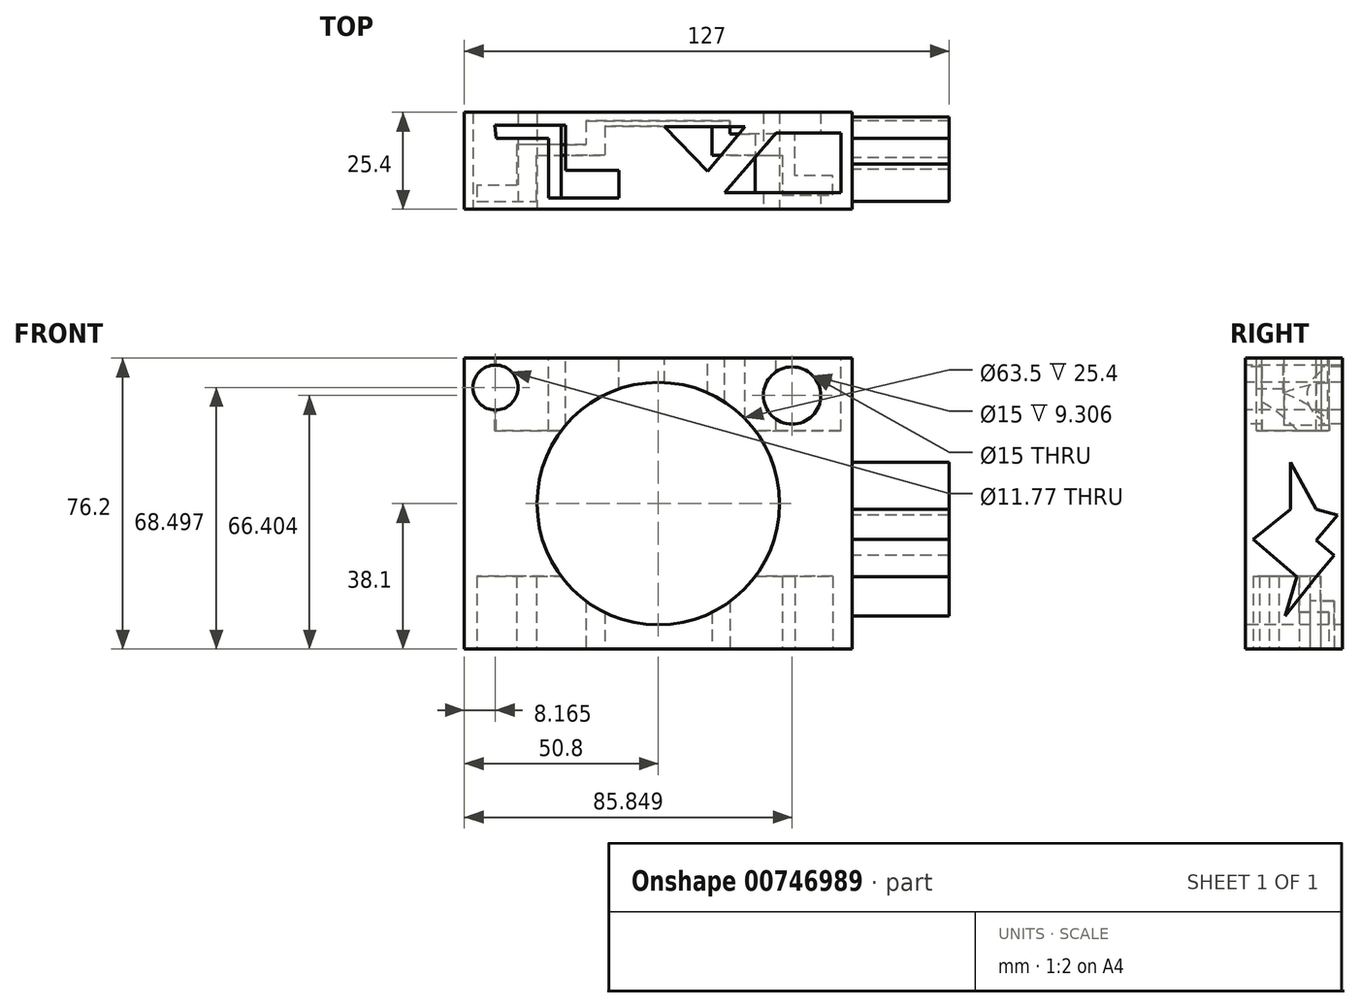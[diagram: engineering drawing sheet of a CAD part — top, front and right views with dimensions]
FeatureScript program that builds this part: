
annotation { "Feature Type Name" : "Feature", "Feature Type Description" : "" }
export const myFeature = defineFeature(function(context is Context, id is Id, definition is map)
    precondition{}
    {
        {
            var Q0;
            Q0=qCreatedBy(makeId("Front.planeOp"),FACE);
            var sketch = newSketch(context, id + "F0", { "sketchPlane" : qUnion([Q0])});
            skLineSegment(sketch, "E0.bottom", {"start": v(0, 0) * mm, "end": v(101.6, 0) * mm});
            skLineSegment(sketch, "E0.top", {"start": v(0, 76.2) * mm, "end": v(101.6, 76.2) * mm});
            skLineSegment(sketch, "E0.left", {"start": v(0, 0) * mm, "end": v(0, 76.2) * mm});
            skLineSegment(sketch, "E0.right", {"start": v(101.6, 0) * mm, "end": v(101.6, 76.2) * mm});
            skSolve(sketch);
        }
        {
            var Q0;
            Q0 = qSketchRegion(id + "F0", true);
            extrude(context, id + "F1", {"entities" : qUnion([Q0]), "depth" : 25.4 * mm, "offsetDistance" : 25.4 * mm});
        }
        {
            var Q0;
            Q0=makeQuery(id+"F1.opExtrude","CAP_FACE",FACE,{"disambiguationData":[OSD([sQuery(id+"F0.wireOp",EDGE,"E0.bottom"),sQuery(id+"F0.wireOp",EDGE,"E0.top"),sQuery(id+"F0.wireOp",EDGE,"E0.left"),sQuery(id+"F0.wireOp",EDGE,"E0.right")])],"isStart":false});
            var sketch = newSketch(context, id + "F2", { "sketchPlane" : qUnion([Q0])});
            skCircle(sketch, "E1", {"center": v(50.8, 38.1) * mm, "radius": 31.75 * mm});
            skPoint(sketch, "E1.centerSnap0", {"position": v(0, 38.1) * mm});
            skSolve(sketch);
        }
        {
            var Q0;
            Q0 = qSketchRegion(id + "F2", true);
            extrude(context, id + "F3", {"entities" : qUnion([Q0]), "operationType" : NewBodyOperationType.ADD, "depth" : 25.4 * mm, "offsetDistance" : 25.4 * mm});
        }
        {
            var Q0;
            Q0=makeQuery(id+"F3.opExtrude","CAP_FACE",FACE,{"disambiguationData":[OSD([sQuery(id+"F2.wireOp",EDGE,"E1")])],"isStart":false});
            extrude(context, id + "F4", {"entities" : qUnion([Q0]), "operationType" : NewBodyOperationType.REMOVE, "endBound" : BoundingType.THROUGH_ALL, "oppositeDirection" : true, "depth" : 25.4 * mm, "offsetDistance" : 25.4 * mm});
        }
        {
            var Q0;
            Q0=makeQuery(id+"F1.opExtrude","CAP_FACE",FACE,{"disambiguationData":[OSD([sQuery(id+"F0.wireOp",EDGE,"E0.bottom"),sQuery(id+"F0.wireOp",EDGE,"E0.top"),sQuery(id+"F0.wireOp",EDGE,"E0.left"),sQuery(id+"F0.wireOp",EDGE,"E0.right")])],"isStart":false});
            var sketch = newSketch(context, id + "F5", { "sketchPlane" : qUnion([Q0])});
            skCircle(sketch, "E2", {"center": v(8.16, 68.5) * mm, "radius": 5.88 * mm});
            skSolve(sketch);
        }
        {
            var Q0;
            Q0=makeQuery(id+"F5.imprint","IMPRINT",FACE,{"disambiguationData":[TD([[makeQuery(id+"F5.imprint","IMPRINT",EDGE,{"derivedFrom":sQuery(id+"F5.wireOp",EDGE,"E2")}),1.0]])]});
            extrude(context, id + "F6", {"entities" : qUnion([Q0]), "operationType" : NewBodyOperationType.REMOVE, "endBound" : BoundingType.THROUGH_ALL, "oppositeDirection" : true, "depth" : 25.4 * mm, "offsetDistance" : 25.4 * mm});
        }
        {
            var Q0;
            Q0=makeQuery(id+"F1.opExtrude","CAP_FACE",FACE,{"disambiguationData":[OSD([sQuery(id+"F0.wireOp",EDGE,"E0.bottom"),sQuery(id+"F0.wireOp",EDGE,"E0.top"),sQuery(id+"F0.wireOp",EDGE,"E0.left"),sQuery(id+"F0.wireOp",EDGE,"E0.right")])],"isStart":false});
            var sketch = newSketch(context, id + "F7", { "sketchPlane" : qUnion([Q0])});
            skCircle(sketch, "E3", {"center": v(85.85, 66.4) * mm, "radius": 7.5 * mm});
            skSolve(sketch);
        }
        {
            var Q0;
            Q0=makeQuery(id+"F7.imprint","IMPRINT",FACE,{"disambiguationData":[TD([[makeQuery(id+"F7.imprint","IMPRINT",EDGE,{"derivedFrom":sQuery(id+"F7.wireOp",EDGE,"E3")}),1.0]])]});
            extrude(context, id + "F8", {"entities" : qUnion([Q0]), "operationType" : NewBodyOperationType.REMOVE, "endBound" : BoundingType.THROUGH_ALL, "oppositeDirection" : true, "depth" : 25.4 * mm, "offsetDistance" : 25.4 * mm});
        }
        {
            var Q0;
            Q0=makeQuery(id+"F1.opExtrude","SWEPT_FACE",FACE,{"disambiguationData":[OSD([sQuery(id+"F0.wireOp",EDGE,"E0.top")])]});
            var sketch = newSketch(context, id + "F9", { "sketchPlane" : qUnion([Q0])});
            skLineSegment(sketch, "E4", {"start": v(52.36, -3.84) * mm, "end": v(73.52, -3.84) * mm});
            skLineSegment(sketch, "E5", {"start": v(73.52, -3.84) * mm, "end": v(63.75, -15.47) * mm});
            skLineSegment(sketch, "E6", {"start": v(52.36, -3.84) * mm, "end": v(63.75, -15.47) * mm});
            skSolve(sketch);
        }
        {
            var Q0;
            Q0=makeQuery(id+"F9.imprint","IMPRINT",FACE,{"disambiguationData":[TD([[makeQuery(id+"F9.imprint","IMPRINT",EDGE,{"derivedFrom":sQuery(id+"F9.wireOp",EDGE,"E4")}),-1.0]])]});
            extrude(context, id + "F10", {"entities" : qUnion([Q0]), "operationType" : NewBodyOperationType.REMOVE, "oppositeDirection" : true, "depth" : 19.05 * mm, "offsetDistance" : 25.4 * mm});
        }
        {
            var Q0;
            Q0=makeQuery(id+"F1.opExtrude","SWEPT_FACE",FACE,{"disambiguationData":[OSD([sQuery(id+"F0.wireOp",EDGE,"E0.top")])]});
            var sketch = newSketch(context, id + "F11", { "sketchPlane" : qUnion([Q0])});
            skLineSegment(sketch, "E7", {"start": v(7.93, -3.37) * mm, "end": v(26.54, -3.37) * mm});
            skLineSegment(sketch, "E8", {"start": v(26.54, -3.37) * mm, "end": v(26.54, -15.23) * mm});
            skLineSegment(sketch, "E9", {"start": v(26.54, -15.23) * mm, "end": v(40.5, -15.23) * mm});
            skLineSegment(sketch, "E10", {"start": v(40.5, -15.23) * mm, "end": v(40.5, -22.44) * mm});
            skLineSegment(sketch, "E11", {"start": v(40.5, -22.44) * mm, "end": v(26.54, -22.44) * mm});
            skLineSegment(sketch, "E12", {"start": v(26.54, -22.44) * mm, "end": v(22.12, -22.44) * mm});
            skLineSegment(sketch, "E13", {"start": v(22.12, -22.44) * mm, "end": v(22.12, -6.86) * mm});
            skLineSegment(sketch, "E14", {"start": v(22.12, -6.86) * mm, "end": v(8.4, -6.86) * mm});
            skLineSegment(sketch, "E15", {"start": v(8.4, -6.86) * mm, "end": v(7.93, -3.37) * mm});
            skSolve(sketch);
        }
        {
            var Q0;
            Q0=makeQuery(id+"F11.imprint","IMPRINT",FACE,{"disambiguationData":[TD([[makeQuery(id+"F11.imprint","IMPRINT",EDGE,{"derivedFrom":sQuery(id+"F11.wireOp",EDGE,"E7")}),-1.0]])]});
            extrude(context, id + "F12", {"entities" : qUnion([Q0]), "operationType" : NewBodyOperationType.REMOVE, "oppositeDirection" : true, "depth" : 19.05 * mm, "offsetDistance" : 25.4 * mm});
        }
        {
            var Q0;
            Q0=makeQuery(id+"F1.opExtrude","SWEPT_FACE",FACE,{"disambiguationData":[OSD([sQuery(id+"F0.wireOp",EDGE,"E0.top")])]});
            var sketch = newSketch(context, id + "F13", { "sketchPlane" : qUnion([Q0])});
            skLineSegment(sketch, "E16", {"start": v(81.66, -5.47) * mm, "end": v(98.64, -5.47) * mm});
            skLineSegment(sketch, "E17", {"start": v(98.64, -5.47) * mm, "end": v(98.64, -21.05) * mm});
            skLineSegment(sketch, "E18", {"start": v(98.64, -21.05) * mm, "end": v(68.17, -21.05) * mm});
            skLineSegment(sketch, "E19", {"start": v(68.17, -21.05) * mm, "end": v(81.66, -5.47) * mm});
            skSolve(sketch);
        }
        {
            var Q0;
            Q0=makeQuery(id+"F13.imprint","IMPRINT",FACE,{"disambiguationData":[TD([[makeQuery(id+"F13.imprint","IMPRINT",EDGE,{"derivedFrom":sQuery(id+"F13.wireOp",EDGE,"E16")}),-1.0]])]});
            extrude(context, id + "F14", {"entities" : qUnion([Q0]), "operationType" : NewBodyOperationType.REMOVE, "oppositeDirection" : true, "depth" : 19.05 * mm, "offsetDistance" : 25.4 * mm});
        }
        {
            var Q0;
            Q0=makeQuery(id+"F1.opExtrude","SWEPT_FACE",FACE,{"disambiguationData":[OSD([sQuery(id+"F0.wireOp",EDGE,"E0.bottom")])]});
            var sketch = newSketch(context, id + "F15", { "sketchPlane" : qUnion([Q0])});
            skLineSegment(sketch, "E20", {"start": v(3.28, 23.38) * mm, "end": v(18.86, 23.38) * mm});
            skLineSegment(sketch, "E21", {"start": v(18.86, 23.38) * mm, "end": v(18.86, 11.28) * mm});
            skLineSegment(sketch, "E22", {"start": v(18.86, 11.28) * mm, "end": v(36.77, 11.28) * mm});
            skLineSegment(sketch, "E23", {"start": v(36.77, 11.28) * mm, "end": v(36.77, 3.6) * mm});
            skLineSegment(sketch, "E24", {"start": v(36.77, 3.6) * mm, "end": v(64.92, 3.6) * mm});
            skLineSegment(sketch, "E25", {"start": v(64.92, 3.6) * mm, "end": v(64.92, 11.28) * mm});
            skLineSegment(sketch, "E26", {"start": v(64.92, 11.28) * mm, "end": v(83.3, 11.28) * mm});
            skLineSegment(sketch, "E27", {"start": v(83.3, 11.28) * mm, "end": v(83.3, 21.75) * mm});
            skLineSegment(sketch, "E28", {"start": v(83.3, 21.75) * mm, "end": v(96.55, 21.75) * mm});
            skLineSegment(sketch, "E29", {"start": v(96.55, 21.75) * mm, "end": v(96.55, 16.63) * mm});
            skLineSegment(sketch, "E30", {"start": v(96.55, 16.63) * mm, "end": v(86.55, 16.63) * mm});
            skLineSegment(sketch, "E31", {"start": v(86.55, 16.63) * mm, "end": v(86.55, 10.58) * mm});
            skLineSegment(sketch, "E32", {"start": v(86.55, 10.58) * mm, "end": v(86.55, 5.7) * mm});
            skLineSegment(sketch, "E33", {"start": v(86.55, 5.7) * mm, "end": v(69.57, 5.7) * mm});
            skLineSegment(sketch, "E34", {"start": v(69.57, 5.7) * mm, "end": v(69.57, 2.2) * mm});
            skLineSegment(sketch, "E35", {"start": v(69.57, 2.2) * mm, "end": v(31.89, 2.2) * mm});
            skLineSegment(sketch, "E36", {"start": v(31.89, 2.2) * mm, "end": v(31.89, 8.49) * mm});
            skLineSegment(sketch, "E37", {"start": v(31.89, 8.49) * mm, "end": v(18.4, 8.49) * mm});
            skLineSegment(sketch, "E38", {"start": v(18.4, 8.49) * mm, "end": v(13.75, 8.49) * mm});
            skLineSegment(sketch, "E39", {"start": v(13.75, 8.49) * mm, "end": v(13.75, 19.19) * mm});
            skLineSegment(sketch, "E40", {"start": v(13.75, 19.19) * mm, "end": v(3.28, 19.19) * mm});
            skLineSegment(sketch, "E41", {"start": v(3.28, 19.19) * mm, "end": v(3.28, 23.38) * mm});
            skSolve(sketch);
        }
        {
            var Q0;
            Q0=makeQuery(id+"F15.imprint","IMPRINT",FACE,{"disambiguationData":[TD([[makeQuery(id+"F15.imprint","IMPRINT",EDGE,{"derivedFrom":sQuery(id+"F15.wireOp",EDGE,"E20")}),-1.0]])]});
            extrude(context, id + "F16", {"entities" : qUnion([Q0]), "operationType" : NewBodyOperationType.REMOVE, "oppositeDirection" : true, "depth" : 19.05 * mm, "offsetDistance" : 25.4 * mm});
        }
        {
            var Q0;
            Q0=makeQuery(id+"F1.opExtrude","SWEPT_FACE",FACE,{"disambiguationData":[OSD([sQuery(id+"F0.wireOp",EDGE,"E0.right")])]});
            var sketch = newSketch(context, id + "F17", { "sketchPlane" : qUnion([Q0])});
            skLineSegment(sketch, "E42", {"start": v(-11.98, 18.96) * mm, "end": v(-23.38, 28.72) * mm});
            skLineSegment(sketch, "E43", {"start": v(-23.38, 28.72) * mm, "end": v(-13.6, 36.63) * mm});
            skLineSegment(sketch, "E44", {"start": v(-13.6, 36.63) * mm, "end": v(-13.6, 48.96) * mm});
            skLineSegment(sketch, "E45", {"start": v(-13.6, 48.96) * mm, "end": v(-6.86, 36.63) * mm});
            skLineSegment(sketch, "E46", {"start": v(-11.98, 18.96) * mm, "end": v(-15, 8.72) * mm});
            skLineSegment(sketch, "E47", {"start": v(-15, 8.72) * mm, "end": v(-6.86, 18.96) * mm});
            skLineSegment(sketch, "E48", {"start": v(-6.86, 18.96) * mm, "end": v(-2.2, 24.54) * mm});
            skLineSegment(sketch, "E49", {"start": v(-2.2, 24.54) * mm, "end": v(-6.86, 28.41) * mm});
            skLineSegment(sketch, "E50", {"start": v(-6.86, 28.41) * mm, "end": v(-1.26, 35.14) * mm});
            skLineSegment(sketch, "E51", {"start": v(-1.26, 35.14) * mm, "end": v(-6.86, 36.63) * mm});
            skSolve(sketch);
        }
        {
            var Q0;
            Q0=makeQuery(id+"F17.imprint","IMPRINT",FACE,{"disambiguationData":[TD([[makeQuery(id+"F17.imprint","IMPRINT",EDGE,{"derivedFrom":sQuery(id+"F17.wireOp",EDGE,"E42")}),-1.0]])]});
            extrude(context, id + "F18", {"entities" : qUnion([Q0]), "operationType" : NewBodyOperationType.ADD, "depth" : 25.4 * mm, "offsetDistance" : 25.4 * mm});
        }
    });
